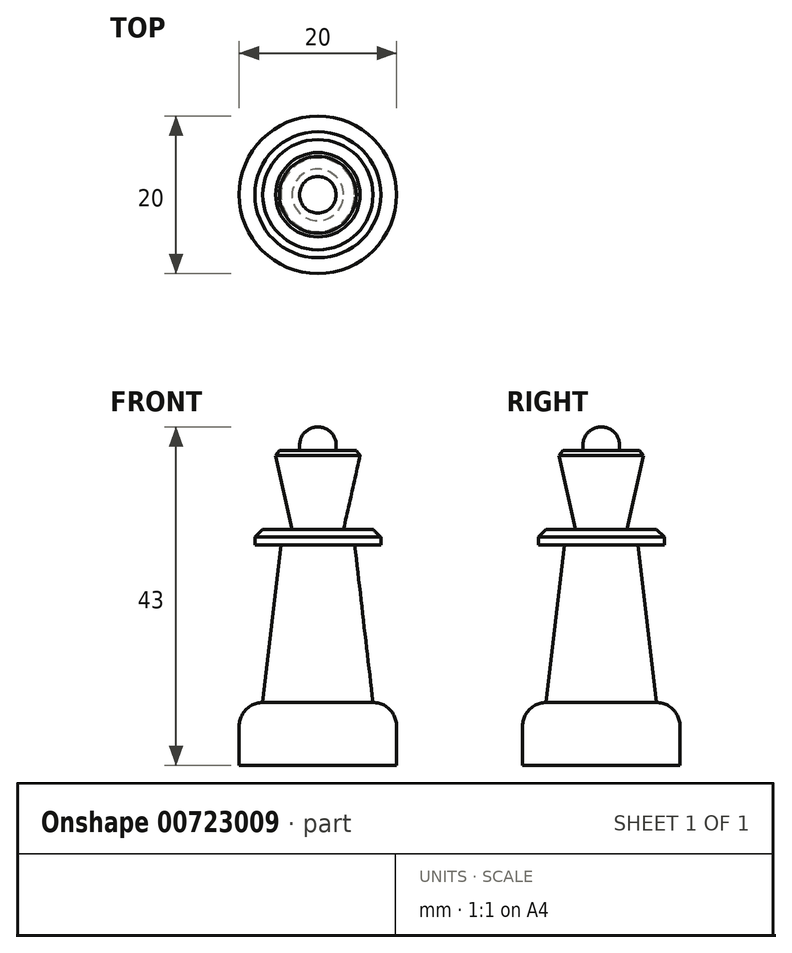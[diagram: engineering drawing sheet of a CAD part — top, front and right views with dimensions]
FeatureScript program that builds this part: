
annotation { "Feature Type Name" : "Feature", "Feature Type Description" : "" }
export const myFeature = defineFeature(function(context is Context, id is Id, definition is map)
    precondition{}
    {
        {
            var Q0;
            Q0=qCreatedBy(makeId("Top.planeOp"),FACE);
            var sketch = newSketch(context, id + "F0", { "sketchPlane" : qUnion([Q0])});
            skCircle(sketch, "E0", {"center": v(0, 0) * mm, "radius": 10 * mm});
            skSolve(sketch);
        }
        {
            var Q0;
            Q0=makeQuery(id+"F0.imprint","IMPRINT",FACE,{"disambiguationData":[TD([[makeQuery(id+"F0.imprint","IMPRINT",EDGE,{"derivedFrom":sQuery(id+"F0.wireOp",EDGE,"E0")}),1.0]])]});
            extrude(context, id + "F1", {"entities" : qUnion([Q0]), "depth" : 5 * mm, "offsetDistance" : 25 * mm});
        }
        {
            var Q0;
            Q0=makeQuery(id+"F1.opExtrude","CAP_FACE",FACE,{"disambiguationData":[OSD([sQuery(id+"F0.wireOp",EDGE,"E0")])],"isStart":false});
            extrude(context, id + "F2", {"entities" : qUnion([Q0]), "operationType" : NewBodyOperationType.ADD, "depth" : 3 * mm, "offsetDistance" : 25 * mm});
        }
        {
            var Q0;
            Q0=makeQuery(id+"F2.opExtrude","CAP_EDGE",EDGE,{"disambiguationData":[OSD([sQuery(id+"F0.wireOp",EDGE,"E0")])],"isStart":false});
            fillet(context, id + "F3", {"entities" : qUnion([Q0]), "radius" : 3 * mm, "tangentPropagation" : true, "allowEdgeOverflow" : false});
        }
        {
            var Q0;
            Q0=makeQuery(id+"F2.opExtrude","CAP_FACE",FACE,{"disambiguationData":[OSD([sQuery(id+"F0.wireOp",EDGE,"E0")])],"isStart":false});
            cPlane(context, id + "F4", {"entities" : qUnion([Q0]), "cplaneType" : CPlaneType.OFFSET, "offset" : 20 * mm, "width" : 150 * mm, "height" : 150 * mm});
        }
        {
            var Q0;
            Q0=qCreatedBy(id+"F4.planeOp",FACE);
            var sketch = newSketch(context, id + "F5", { "sketchPlane" : qUnion([Q0])});
            skPoint(sketch, "E1", {"position": v(0, 0) * mm});
            skCircle(sketch, "E2", {"center": v(0, 0) * mm, "radius": 4.68 * mm});
            skSolve(sketch);
        }
        {
            var Q1;
            Q1=makeQuery(id+"F2.opExtrude","CAP_FACE",FACE,{"disambiguationData":[OSD([sQuery(id+"F0.wireOp",EDGE,"E0")])],"isStart":false});
            var Q2;
            Q2=makeQuery(id+"F5.imprint","IMPRINT",FACE,{"disambiguationData":[TD([[makeQuery(id+"F5.imprint","IMPRINT",EDGE,{"derivedFrom":sQuery(id+"F5.wireOp",EDGE,"E2")}),1.0]])]});
            loft(context, id + "F6", {"operationType" : NewBodyOperationType.ADD, "sheetProfilesArray" : [{ "sheetProfileEntities" : qUnion([Q1]) }, { "sheetProfileEntities" : qUnion([Q2]) }]});
        }
        {
            var Q0;
            Q0=makeQuery(id+"F6.opLoft","CAP_FACE",FACE,{"disambiguationData":[OSD([makeQuery(id+"F5.imprint","IMPRINT",FACE,{"disambiguationData":[TD([[makeQuery(id+"F5.imprint","IMPRINT",EDGE,{"derivedFrom":sQuery(id+"F5.wireOp",EDGE,"E2")}),1.0]])]})])],"isStart":true});
            var sketch = newSketch(context, id + "F7", { "sketchPlane" : qUnion([Q0])});
            skCircle(sketch, "E3", {"center": v(0, 0) * mm, "radius": 8 * mm});
            skSolve(sketch);
        }
        {
            var Q0;
            Q0=makeQuery(id+"F7.imprint","IMPRINT",FACE,{"disambiguationData":[TD([[makeQuery(id+"F7.imprint","IMPRINT",EDGE,{"derivedFrom":sQuery(id+"F7.wireOp",EDGE,"E3")}),1.0]])]});
            var Q1;
            Q1=makeQuery(id+"F7.imprint","IMPRINT",FACE,{"disambiguationData":[TD([[makeQuery(id+"F7.imprint","IMPRINT",EDGE,{"derivedFrom":makeQuery(id+"F6.opLoft","MID_CAP_EDGE",EDGE,{"disambiguationData":[OSD([sQuery(id+"F5.wireOp",EDGE,"E2")])],"capPos":1.0})}),1.0]])]});
            extrude(context, id + "F8", {"entities" : qUnion([Q0, Q1]), "operationType" : NewBodyOperationType.ADD, "depth" : 2 * mm, "offsetDistance" : 25 * mm});
        }
        {
            var Q0;
            Q0=makeQuery(id+"F8.opExtrude","CAP_EDGE",EDGE,{"disambiguationData":[OSD([sQuery(id+"F7.wireOp",EDGE,"E3")])],"isStart":false});
            chamfer(context, id + "F9", {"entities" : qUnion([Q0]), "width" : 1 * mm, "tangentPropagation" : true});
        }
        {
            var Q0;
            Q0=makeQuery(id+"F8.opExtrude","CAP_FACE",FACE,{"disambiguationData":[OSD([sQuery(id+"F7.wireOp",EDGE,"E3")])],"isStart":false});
            var sketch = newSketch(context, id + "F10", { "sketchPlane" : qUnion([Q0])});
            skCircle(sketch, "E4", {"center": v(0, 0) * mm, "radius": 3.27 * mm});
            skSolve(sketch);
        }
        {
            var Q0;
            Q0=makeQuery(id+"F10.imprint","IMPRINT",FACE,{"disambiguationData":[TD([[makeQuery(id+"F10.imprint","IMPRINT",EDGE,{"derivedFrom":sQuery(id+"F10.wireOp",EDGE,"E4")}),1.0]])]});
            cPlane(context, id + "F11", {"entities" : qUnion([Q0]), "cplaneType" : CPlaneType.OFFSET, "offset" : 10 * mm, "width" : 150 * mm, "height" : 150 * mm});
        }
        {
            var Q0;
            Q0=qCreatedBy(id+"F11.planeOp",FACE);
            var sketch = newSketch(context, id + "F12", { "sketchPlane" : qUnion([Q0])});
            skCircle(sketch, "E5", {"center": v(0, 0) * mm, "radius": 5.5 * mm});
            skSolve(sketch);
        }
        {
            var Q1;
            Q1=makeQuery(id+"F10.imprint","IMPRINT",FACE,{"disambiguationData":[TD([[makeQuery(id+"F10.imprint","IMPRINT",EDGE,{"derivedFrom":sQuery(id+"F10.wireOp",EDGE,"E4")}),1.0]])]});
            var Q2;
            Q2=makeQuery(id+"F12.imprint","IMPRINT",FACE,{"disambiguationData":[TD([[makeQuery(id+"F12.imprint","IMPRINT",EDGE,{"derivedFrom":sQuery(id+"F12.wireOp",EDGE,"E5")}),1.0]])]});
            loft(context, id + "F13", {"operationType" : NewBodyOperationType.ADD, "sheetProfilesArray" : [{ "sheetProfileEntities" : qUnion([Q1]) }, { "sheetProfileEntities" : qUnion([Q2]) }]});
        }
        {
            var Q0;
            Q0=makeQuery(id+"F13.opLoft","MID_CAP_EDGE",EDGE,{"disambiguationData":[OSD([sQuery(id+"F12.wireOp",EDGE,"E5")])],"capPos":1.0});
            chamfer(context, id + "F14", {"entities" : qUnion([Q0]), "width" : 0.5 * mm, "tangentPropagation" : true});
        }
        {
            var Q0;
            Q0=makeQuery(id+"F13.opLoft","CAP_FACE",FACE,{"disambiguationData":[OSD([makeQuery(id+"F12.imprint","IMPRINT",FACE,{"disambiguationData":[TD([[makeQuery(id+"F12.imprint","IMPRINT",EDGE,{"derivedFrom":sQuery(id+"F12.wireOp",EDGE,"E5")}),1.0]])]})])],"isStart":true});
            var sketch = newSketch(context, id + "F15", { "sketchPlane" : qUnion([Q0])});
            skCircle(sketch, "E6", {"center": v(0, 0) * mm, "radius": 2.32 * mm});
            skSolve(sketch);
        }
        {
            var Q0;
            Q0=makeQuery(id+"F15.imprint","IMPRINT",FACE,{"disambiguationData":[TD([[makeQuery(id+"F15.imprint","IMPRINT",EDGE,{"derivedFrom":sQuery(id+"F15.wireOp",EDGE,"E6")}),1.0]])]});
            extrude(context, id + "F16", {"entities" : qUnion([Q0]), "operationType" : NewBodyOperationType.ADD, "depth" : 3 * mm, "offsetDistance" : 25 * mm});
        }
        {
            var Q0;
            Q0=makeQuery(id+"F16.opExtrude","CAP_FACE",FACE,{"disambiguationData":[OSD([sQuery(id+"F15.wireOp",EDGE,"E6")])],"isStart":false});
            fillet(context, id + "F17", {"entities" : qUnion([Q0]), "radius" : 2.3 * mm, "tangentPropagation" : true, "allowEdgeOverflow" : false});
        }
    });
